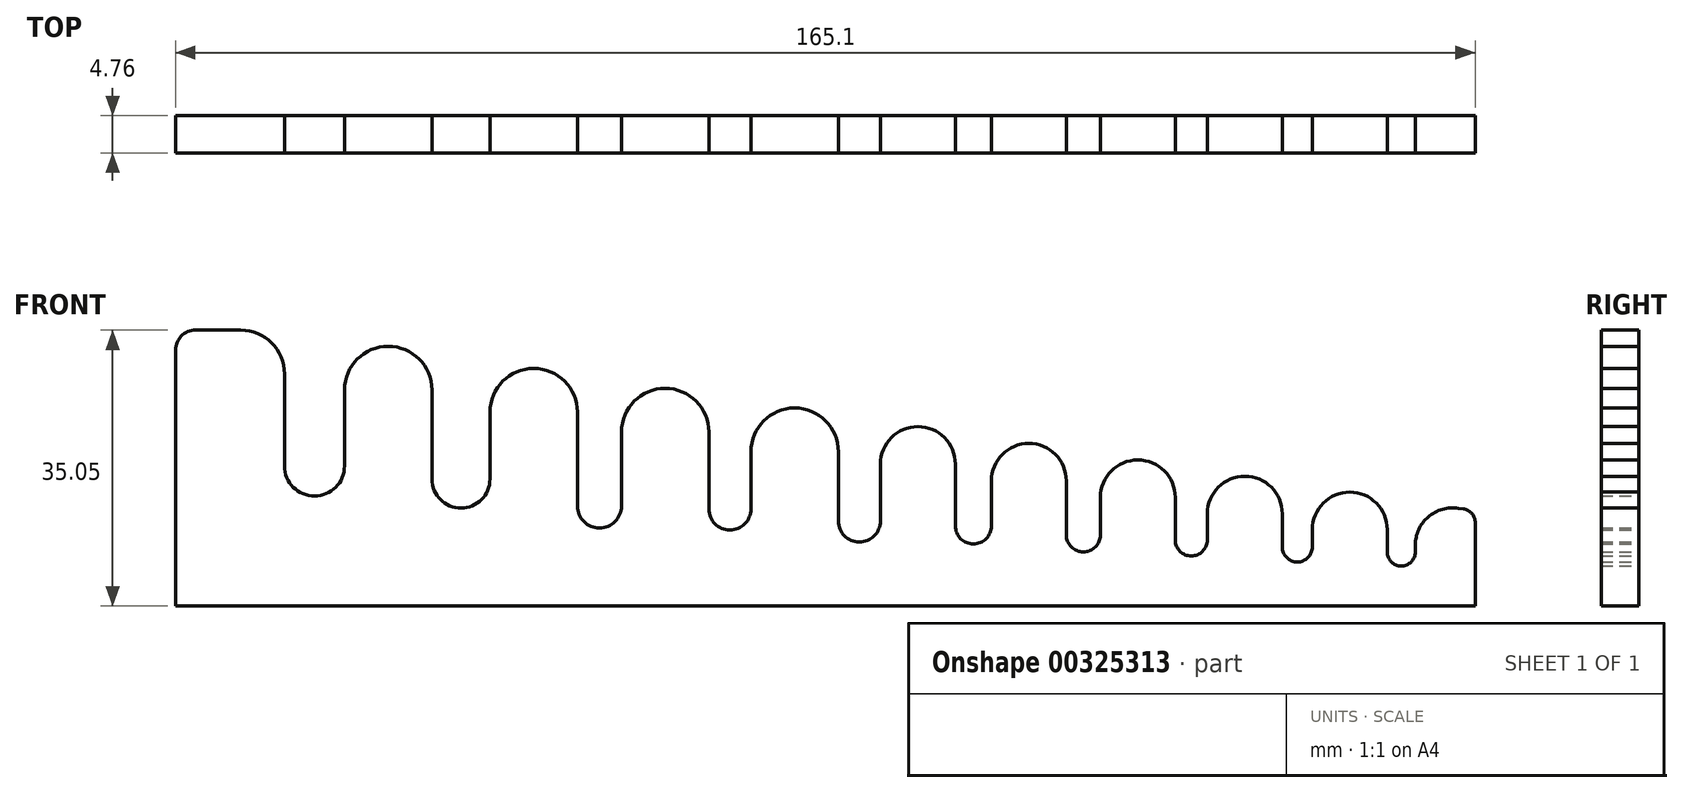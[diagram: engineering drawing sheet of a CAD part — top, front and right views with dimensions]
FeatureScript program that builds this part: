
annotation { "Feature Type Name" : "Feature", "Feature Type Description" : "" }
export const myFeature = defineFeature(function(context is Context, id is Id, definition is map)
    precondition{}
    {
        {
            var Q0;
            Q0=qCreatedBy(makeId("Front.planeOp"),FACE);
            var sketch = newSketch(context, id + "F0", { "sketchPlane" : qUnion([Q0])});
            skLineSegment(sketch, "E0", {"start": v(0, 0) * mm, "end": v(0, 32.51) * mm});
            skLineSegment(sketch, "E1", {"start": v(2.54, 35.05) * mm, "end": v(8.29, 35.05) * mm});
            skLineSegment(sketch, "E2", {"start": v(27.85, 32.93) * mm, "end": v(27.85, 32.93) * mm});
            skLineSegment(sketch, "E3", {"start": v(165.1, 10.57) * mm, "end": v(165.1, 0) * mm});
            skLineSegment(sketch, "E4", {"start": v(165.1, 0) * mm, "end": v(0, 0) * mm});
            skLineSegment(sketch, "E5", {"start": v(13.84, 29.5) * mm, "end": v(13.84, 17.78) * mm});
            skLineSegment(sketch, "E6", {"start": v(17.65, 13.97) * mm, "end": v(17.65, 13.97) * mm});
            skLineSegment(sketch, "E7", {"start": v(21.46, 17.78) * mm, "end": v(21.46, 27.43) * mm});
            skLineSegment(sketch, "E8", {"start": v(51.05, 24.63) * mm, "end": v(51.05, 12.7) * mm});
            skLineSegment(sketch, "E9", {"start": v(53.85, 9.9) * mm, "end": v(53.85, 9.9) * mm});
            skLineSegment(sketch, "E10", {"start": v(56.64, 12.7) * mm, "end": v(56.64, 22.1) * mm});
            skLineSegment(sketch, "E11.trimOffspring", {"start": v(63.03, 27.59) * mm, "end": v(63.03, 27.59) * mm});
            skLineSegment(sketch, "E12", {"start": v(84.2, 19.6) * mm, "end": v(84.2, 10.8) * mm});
            skLineSegment(sketch, "E13", {"start": v(86.87, 8.13) * mm, "end": v(86.87, 8.13) * mm});
            skLineSegment(sketch, "E14", {"start": v(89.53, 10.8) * mm, "end": v(89.53, 18.03) * mm});
            skLineSegment(sketch, "E15", {"start": v(113.16, 15.89) * mm, "end": v(113.16, 9.02) * mm});
            skLineSegment(sketch, "E16", {"start": v(115.32, 6.86) * mm, "end": v(115.32, 6.86) * mm});
            skLineSegment(sketch, "E17", {"start": v(117.47, 9.02) * mm, "end": v(117.47, 13.79) * mm});
            skLineSegment(sketch, "E18", {"start": v(140.59, 11.72) * mm, "end": v(140.59, 7.5) * mm});
            skLineSegment(sketch, "E19", {"start": v(142.5, 5.59) * mm, "end": v(142.5, 5.59) * mm});
            skLineSegment(sketch, "E20", {"start": v(144.4, 7.5) * mm, "end": v(144.4, 9.7) * mm});
            skLineSegment(sketch, "E21", {"start": v(153.92, 9.7) * mm, "end": v(153.92, 6.86) * mm});
            skLineSegment(sketch, "E22", {"start": v(155.7, 5.08) * mm, "end": v(155.7, 5.08) * mm});
            skLineSegment(sketch, "E23", {"start": v(157.48, 6.86) * mm, "end": v(157.48, 7.72) * mm});
            skLineSegment(sketch, "E24.trimOffspring", {"start": v(149.88, 14.4) * mm, "end": v(149.88, 14.4) * mm});
            skLineSegment(sketch, "E25.trimOffspring", {"start": v(162.96, 12.42) * mm, "end": v(163.59, 12.33) * mm});
            skLineSegment(sketch, "E26", {"start": v(95.01, 22.73) * mm, "end": v(95.01, 22.73) * mm});
            skLineSegment(sketch, "E27", {"start": v(122.95, 18.5) * mm, "end": v(122.95, 18.5) * mm});
            skLineSegment(sketch, "E28", {"start": v(32.58, 27.43) * mm, "end": v(32.58, 16.13) * mm});
            skLineSegment(sketch, "E29", {"start": v(36.26, 12.45) * mm, "end": v(36.26, 12.45) * mm});
            skLineSegment(sketch, "E30", {"start": v(39.94, 16.13) * mm, "end": v(39.94, 24.63) * mm});
            skLineSegment(sketch, "E31.trimOffspring", {"start": v(46.33, 30.12) * mm, "end": v(46.33, 30.12) * mm});
            skLineSegment(sketch, "E32", {"start": v(67.75, 22.1) * mm, "end": v(67.75, 12.32) * mm});
            skLineSegment(sketch, "E33", {"start": v(70.42, 9.65) * mm, "end": v(70.42, 9.65) * mm});
            skLineSegment(sketch, "E34", {"start": v(73.09, 12.32) * mm, "end": v(73.09, 19.6) * mm});
            skLineSegment(sketch, "E35.trimOffspring", {"start": v(79.48, 25.1) * mm, "end": v(79.48, 25.1) * mm});
            skLineSegment(sketch, "E36", {"start": v(99.06, 18.03) * mm, "end": v(99.06, 10.16) * mm});
            skLineSegment(sketch, "E37", {"start": v(101.35, 7.87) * mm, "end": v(101.35, 7.87) * mm});
            skLineSegment(sketch, "E38", {"start": v(103.63, 10.16) * mm, "end": v(103.63, 15.89) * mm});
            skLineSegment(sketch, "E39.trimOffspring", {"start": v(109.1, 20.6) * mm, "end": v(109.1, 20.6) * mm});
            skLineSegment(sketch, "E40", {"start": v(127, 13.79) * mm, "end": v(127, 8.38) * mm});
            skLineSegment(sketch, "E41", {"start": v(129.03, 6.35) * mm, "end": v(129.03, 6.35) * mm});
            skLineSegment(sketch, "E42", {"start": v(131.06, 8.38) * mm, "end": v(131.06, 11.72) * mm});
            skLineSegment(sketch, "E43.trimOffspring", {"start": v(136.54, 16.43) * mm, "end": v(136.54, 16.43) * mm});
            skPoint(sketch, "E44.visualSharp", {"position": v(13.84, 13.97) * mm});
            skArc(sketch, "E44.filletArc", {"start": v(13.84, 17.78) * mm, "mid": v(14.96, 15.09) * mm, "end": v(17.65, 13.97) * mm});
            skPoint(sketch, "E45.visualSharp", {"position": v(21.46, 13.97) * mm});
            skArc(sketch, "E45.filletArc", {"start": v(17.65, 13.97) * mm, "mid": v(20.35, 15.09) * mm, "end": v(21.46, 17.78) * mm});
            skPoint(sketch, "E46.visualSharp", {"position": v(32.58, 12.45) * mm});
            skArc(sketch, "E46.filletArc", {"start": v(32.58, 16.13) * mm, "mid": v(33.65, 13.52) * mm, "end": v(36.26, 12.45) * mm});
            skPoint(sketch, "E47.visualSharp", {"position": v(39.94, 12.45) * mm});
            skArc(sketch, "E47.filletArc", {"start": v(36.26, 12.45) * mm, "mid": v(38.86, 13.52) * mm, "end": v(39.94, 16.13) * mm});
            skPoint(sketch, "E48.visualSharp", {"position": v(51.05, 9.9) * mm});
            skArc(sketch, "E48.filletArc", {"start": v(51.05, 12.7) * mm, "mid": v(51.87, 10.72) * mm, "end": v(53.85, 9.9) * mm});
            skPoint(sketch, "E49.visualSharp", {"position": v(56.64, 9.9) * mm});
            skArc(sketch, "E49.filletArc", {"start": v(53.85, 9.9) * mm, "mid": v(55.82, 10.72) * mm, "end": v(56.64, 12.7) * mm});
            skPoint(sketch, "E50.visualSharp", {"position": v(67.75, 9.65) * mm});
            skArc(sketch, "E50.filletArc", {"start": v(67.75, 12.32) * mm, "mid": v(68.54, 10.43) * mm, "end": v(70.42, 9.65) * mm});
            skPoint(sketch, "E51.visualSharp", {"position": v(73.09, 9.65) * mm});
            skArc(sketch, "E51.filletArc", {"start": v(70.42, 9.65) * mm, "mid": v(72.3, 10.43) * mm, "end": v(73.09, 12.32) * mm});
            skPoint(sketch, "E52.visualSharp", {"position": v(84.2, 8.13) * mm});
            skArc(sketch, "E52.filletArc", {"start": v(84.2, 10.8) * mm, "mid": v(84.98, 8.9) * mm, "end": v(86.87, 8.13) * mm});
            skPoint(sketch, "E53.visualSharp", {"position": v(89.53, 8.13) * mm});
            skArc(sketch, "E53.filletArc", {"start": v(86.87, 8.13) * mm, "mid": v(88.75, 8.9) * mm, "end": v(89.53, 10.8) * mm});
            skPoint(sketch, "E54.visualSharp", {"position": v(99.06, 7.87) * mm});
            skArc(sketch, "E54.filletArc", {"start": v(99.06, 10.16) * mm, "mid": v(99.73, 8.54) * mm, "end": v(101.35, 7.87) * mm});
            skPoint(sketch, "E55.visualSharp", {"position": v(103.63, 7.87) * mm});
            skArc(sketch, "E55.filletArc", {"start": v(101.35, 7.87) * mm, "mid": v(102.96, 8.54) * mm, "end": v(103.63, 10.16) * mm});
            skPoint(sketch, "E56.visualSharp", {"position": v(113.16, 6.86) * mm});
            skArc(sketch, "E56.filletArc", {"start": v(113.16, 9.02) * mm, "mid": v(113.79, 7.5) * mm, "end": v(115.32, 6.86) * mm});
            skPoint(sketch, "E57.visualSharp", {"position": v(117.48, 6.86) * mm});
            skArc(sketch, "E57.filletArc", {"start": v(115.32, 6.86) * mm, "mid": v(116.84, 7.5) * mm, "end": v(117.47, 9.02) * mm});
            skPoint(sketch, "E58.visualSharp", {"position": v(127, 6.35) * mm});
            skArc(sketch, "E58.filletArc", {"start": v(127, 8.38) * mm, "mid": v(127.6, 6.95) * mm, "end": v(129.03, 6.35) * mm});
            skPoint(sketch, "E59.visualSharp", {"position": v(131.06, 6.35) * mm});
            skArc(sketch, "E59.filletArc", {"start": v(129.03, 6.35) * mm, "mid": v(130.47, 6.95) * mm, "end": v(131.06, 8.38) * mm});
            skPoint(sketch, "E60.visualSharp", {"position": v(140.59, 5.59) * mm});
            skArc(sketch, "E60.filletArc", {"start": v(140.59, 7.5) * mm, "mid": v(141.15, 6.15) * mm, "end": v(142.5, 5.59) * mm});
            skPoint(sketch, "E61.visualSharp", {"position": v(144.4, 5.59) * mm});
            skArc(sketch, "E61.filletArc", {"start": v(142.5, 5.59) * mm, "mid": v(143.84, 6.15) * mm, "end": v(144.4, 7.5) * mm});
            skPoint(sketch, "E62.visualSharp", {"position": v(153.92, 5.08) * mm});
            skArc(sketch, "E62.filletArc", {"start": v(153.92, 6.86) * mm, "mid": v(154.44, 5.6) * mm, "end": v(155.7, 5.08) * mm});
            skPoint(sketch, "E63.visualSharp", {"position": v(157.48, 5.08) * mm});
            skArc(sketch, "E63.filletArc", {"start": v(155.7, 5.08) * mm, "mid": v(156.96, 5.6) * mm, "end": v(157.48, 6.86) * mm});
            skPoint(sketch, "E64.visualSharp", {"position": v(21.46, 33.9) * mm});
            skArc(sketch, "E64.filletArc", {"start": v(27.85, 32.93) * mm, "mid": v(23.4, 31.65) * mm, "end": v(21.46, 27.43) * mm});
            skPoint(sketch, "E65.visualSharp", {"position": v(32.58, 32.2) * mm});
            skArc(sketch, "E65.filletArc", {"start": v(32.58, 27.43) * mm, "mid": v(31.23, 31.05) * mm, "end": v(27.85, 32.93) * mm});
            skPoint(sketch, "E66.visualSharp", {"position": v(39.94, 31.1) * mm});
            skArc(sketch, "E66.filletArc", {"start": v(46.33, 30.12) * mm, "mid": v(41.88, 28.84) * mm, "end": v(39.94, 24.63) * mm});
            skPoint(sketch, "E67.visualSharp", {"position": v(51.05, 29.4) * mm});
            skArc(sketch, "E67.filletArc", {"start": v(51.05, 24.63) * mm, "mid": v(49.71, 28.25) * mm, "end": v(46.33, 30.12) * mm});
            skPoint(sketch, "E68.visualSharp", {"position": v(67.75, 26.87) * mm});
            skArc(sketch, "E68.filletArc", {"start": v(67.75, 22.1) * mm, "mid": v(66.41, 25.72) * mm, "end": v(63.03, 27.59) * mm});
            skPoint(sketch, "E69.visualSharp", {"position": v(56.64, 28.56) * mm});
            skArc(sketch, "E69.filletArc", {"start": v(63.03, 27.59) * mm, "mid": v(58.58, 26.3) * mm, "end": v(56.64, 22.1) * mm});
            skPoint(sketch, "E70.visualSharp", {"position": v(73.09, 26.06) * mm});
            skArc(sketch, "E70.filletArc", {"start": v(79.48, 25.1) * mm, "mid": v(75.02, 23.81) * mm, "end": v(73.09, 19.6) * mm});
            skPoint(sketch, "E71.visualSharp", {"position": v(84.2, 24.38) * mm});
            skArc(sketch, "E71.filletArc", {"start": v(84.2, 19.6) * mm, "mid": v(82.86, 23.22) * mm, "end": v(79.48, 25.1) * mm});
            skPoint(sketch, "E72.visualSharp", {"position": v(89.53, 23.57) * mm});
            skArc(sketch, "E72.filletArc", {"start": v(95.01, 22.73) * mm, "mid": v(91.2, 21.64) * mm, "end": v(89.53, 18.03) * mm});
            skPoint(sketch, "E73.visualSharp", {"position": v(99.06, 22.12) * mm});
            skArc(sketch, "E73.filletArc", {"start": v(99.06, 18.03) * mm, "mid": v(97.9, 21.13) * mm, "end": v(95.01, 22.73) * mm});
            skPoint(sketch, "E74.visualSharp", {"position": v(103.63, 21.43) * mm});
            skArc(sketch, "E74.filletArc", {"start": v(109.1, 20.6) * mm, "mid": v(105.29, 19.5) * mm, "end": v(103.63, 15.89) * mm});
            skPoint(sketch, "E75.visualSharp", {"position": v(113.16, 19.98) * mm});
            skArc(sketch, "E75.filletArc", {"start": v(113.16, 15.89) * mm, "mid": v(112, 19) * mm, "end": v(109.1, 20.6) * mm});
            skPoint(sketch, "E76.visualSharp", {"position": v(117.47, 19.33) * mm});
            skArc(sketch, "E76.filletArc", {"start": v(122.95, 18.5) * mm, "mid": v(119.13, 17.4) * mm, "end": v(117.47, 13.79) * mm});
            skPoint(sketch, "E77.visualSharp", {"position": v(127, 17.88) * mm});
            skArc(sketch, "E77.filletArc", {"start": v(127, 13.79) * mm, "mid": v(125.85, 16.9) * mm, "end": v(122.95, 18.5) * mm});
            skPoint(sketch, "E78.visualSharp", {"position": v(131.06, 17.26) * mm});
            skArc(sketch, "E78.filletArc", {"start": v(136.54, 16.43) * mm, "mid": v(132.72, 15.34) * mm, "end": v(131.06, 11.72) * mm});
            skPoint(sketch, "E79.visualSharp", {"position": v(140.59, 15.82) * mm});
            skArc(sketch, "E79.filletArc", {"start": v(140.59, 11.72) * mm, "mid": v(139.44, 14.83) * mm, "end": v(136.54, 16.43) * mm});
            skPoint(sketch, "E80.visualSharp", {"position": v(144.4, 15.24) * mm});
            skArc(sketch, "E80.filletArc", {"start": v(149.88, 14.4) * mm, "mid": v(146.06, 13.31) * mm, "end": v(144.4, 9.7) * mm});
            skPoint(sketch, "E81.visualSharp", {"position": v(153.92, 13.8) * mm});
            skArc(sketch, "E81.filletArc", {"start": v(153.92, 9.7) * mm, "mid": v(152.77, 12.8) * mm, "end": v(149.88, 14.4) * mm});
            skPoint(sketch, "E82.visualSharp", {"position": v(13.84, 35.05) * mm});
            skArc(sketch, "E82.filletArc", {"start": v(13.84, 29.5) * mm, "mid": v(12.22, 33.42) * mm, "end": v(8.29, 35.05) * mm});
            skPoint(sketch, "E83.visualSharp", {"position": v(157.48, 13.25) * mm});
            skArc(sketch, "E83.filletArc", {"start": v(162.96, 12.42) * mm, "mid": v(159.14, 11.33) * mm, "end": v(157.48, 7.72) * mm});
            skPoint(sketch, "E84.visualSharp", {"position": v(165.1, 12.1) * mm});
            skArc(sketch, "E84.filletArc", {"start": v(165.1, 10.57) * mm, "mid": v(164.67, 11.73) * mm, "end": v(163.59, 12.33) * mm});
            skPoint(sketch, "E85.visualSharp", {"position": v(0, 35.05) * mm});
            skArc(sketch, "E85.filletArc", {"start": v(2.54, 35.05) * mm, "mid": v(0.74, 34.3) * mm, "end": v(0, 32.51) * mm});
            skSolve(sketch);
        }
        {
            var Q0;
            Q0 = qSketchRegion(id + "F0", true);
            extrude(context, id + "F1", {"entities" : qUnion([Q0]), "depth" : 4.76 * mm});
        }
    });
